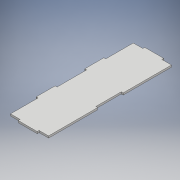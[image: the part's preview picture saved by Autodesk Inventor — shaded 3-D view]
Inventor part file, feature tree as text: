
AUTODESK INVENTOR PART (.ipt)
format: ipt  version: 2017 (Build 210142000, 142)  size: 137,728 bytes
history: native  units: mm
features: extrude x1, sketch x1
ambient origin geometry x8: Origin, YZ Plane, XZ Plane, XY Plane, X Axis, Y Axis, Z Axis, Center Point
bodies: Solid1 (feature_tree)
feature tree (2):
  extrude  "Extrusion1"  Depth=77.0mm
  sketch  "Sketch1"  dims[d23=3.0mm d24=0.0mm d25=193.0mm d26=60.0mm d27=3.0mm d28=30.0mm d29=15.0mm d30=3.0mm d31=3.0mm d32=15.0mm d33=3.0mm d34=3.0mm d35=3.0mm d36=3.0mm d37=15.0mm d38=40.0mm d39=3.0mm d41=77.0mm d43=3.0mm d44=76.0mm d45=199.145723mm d46=43.3mm d47=46.6mm d48=43.3mm d49=30.0mm d50=29.8mm]
